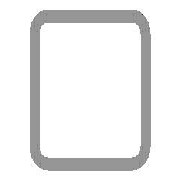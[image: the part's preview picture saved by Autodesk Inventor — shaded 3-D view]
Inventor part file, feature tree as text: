
AUTODESK INVENTOR PART (.ipt)
format: ipt  version: 2022 (Build 260153000, 153)  size: 175,616 bytes
history: native  units: mm (DEFAULTED — no unit token found)
features: other x5, sketch x2, sweep x1, plane x1
ambient origin geometry x8: Origin, YZ Plane, XZ Plane, XY Plane, X Axis, Y Axis, Z Axis, Center Point
bodies: Solid1 (feature_tree), Body (feature_tree)
feature tree (9):
  parser-record x1  (decoder bookkeeping rows leaked as tree rows — omitted from the tree; the rows remain in map.json)
  other  "Driven Length"
  other  "Start Plane"
  other  "End Plane"
  sweep  "Sweep Path"
  other  "Orientation Work Plane"
  sketch  "Sketch3"  dims[d7=8.0mm d9=40.0mm]
  plane  "Work Plane3"
  sketch  "Sketch4"  dims[d11=40.0mm d12=4.0mm d13=-0.0mm d14=3515.406592mm d15=20.0mm d16=20.0mm d17=90.0deg d18=3515.406592mm d19=0.0mm d20=0.0mm]
